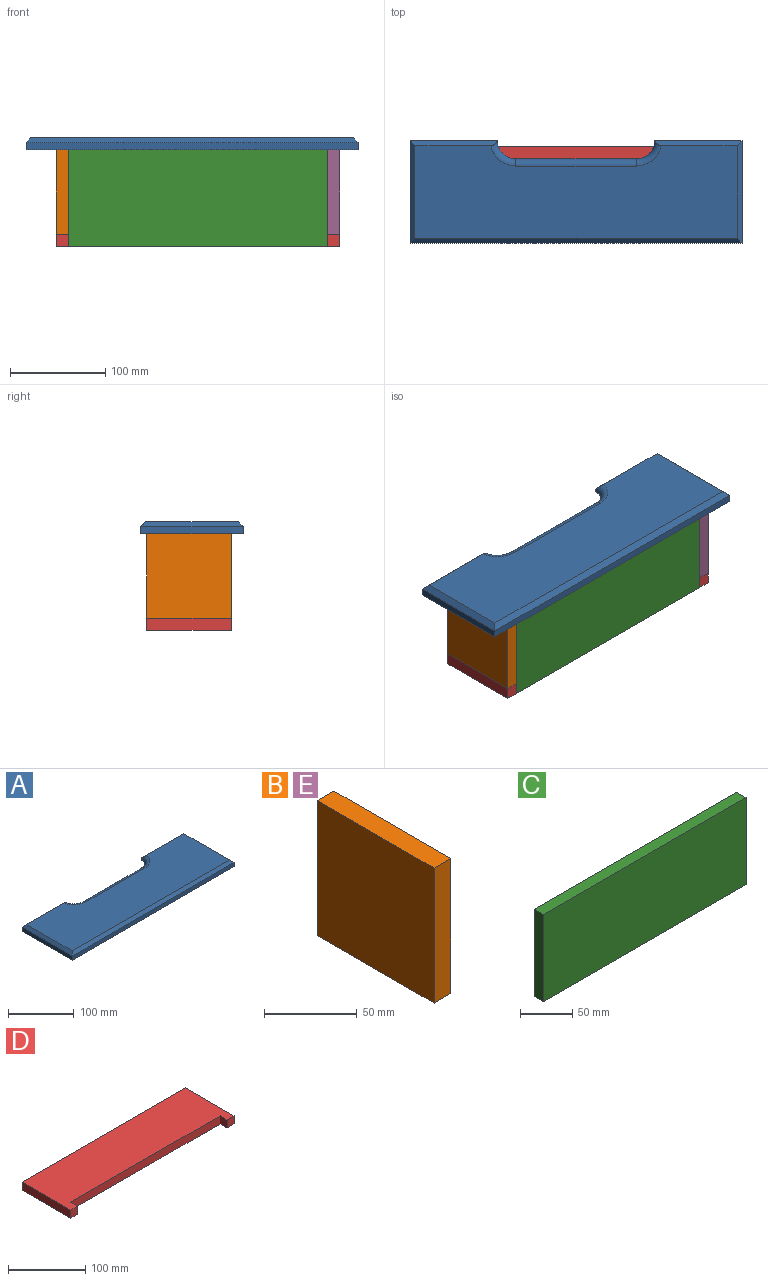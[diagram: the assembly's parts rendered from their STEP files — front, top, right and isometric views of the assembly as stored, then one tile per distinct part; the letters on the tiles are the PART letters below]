
ASSEMBLY  parts=5 mates=4
PART A: 18 faces, bbox 349.3x108x12.7 mm
  f0: plane 91.97x7.62mm, normal (0,1,0), area 688.9mm2, adj f4,f6,f7,f8,f17
  f1: plane 91.97x7.62mm, normal (0,1,0), area 688.9mm2, adj f2,f6,f11,f12,f13
  f2: plane 107.95x7.62mm, normal (-1,0,0), area 822.6mm2, adj f1,f3,f6,f14
  f3: plane 349.25x7.62mm, normal (0,-1,0), area 2661.3mm2, adj f2,f4,f6,f15
  f4: plane 107.95x7.62mm, normal (1,0,0), area 822.6mm2, adj f0,f3,f6,f16
  f5: plane 339.09x97.79mm, normal (0,0,1), area 29569.7mm2, adj f7,f9,f11,f13,f14,f15,f16,f17
  f6: plane 349.25x107.95mm, normal (0,0,-1), area 33197.2mm2, adj f0,f1,f2,f3,f4,f8,f10,f12
  f7: torus R=26.67mm, axis (0,0,1), area 340.9mm2, adj f0,f5,f8,f9,f17
  f8: torus R=26.67mm, axis (0,0,1), area 372mm2, adj f0,f6,f7,f10
  f9: cylinder r=7.62mm len=127mm, axis (1,0,0), area 1358.1mm2, adj f5,f7,f10,f11
  f10: cylinder r=7.62mm len=127mm, axis (-1,0,0), area 1358.1mm2, adj f6,f8,f9,f12
  f11: torus R=26.67mm, axis (0,0,1), area 340.9mm2, adj f1,f5,f9,f12,f13
  f12: torus R=26.67mm, axis (0,0,1), area 372mm2, adj f1,f6,f10,f11
  f13: plane 91.64x5.08mm, normal (0,0.71,0.71), area 627.5mm2, adj f1,f5,f11,f14
  f14: plane 107.95x5.08mm, normal (-0.71,0,0.71), area 739mm2, adj f2,f5,f13,f15
  f15: plane 349.25x5.08mm, normal (0,-0.71,0.71), area 2472.6mm2, adj f3,f5,f14,f16
  f16: plane 107.95x5.08mm, normal (0.71,0,0.71), area 739mm2, adj f4,f5,f15,f17
  f17: plane 91.64x5.08mm, normal (0,0.71,0.71), area 627.5mm2, adj f0,f5,f7,f16
PART B: 6 faces, bbox 12.7x88.9x88.9 mm
  f0: plane 88.9x12.7mm, normal (0,0,-1), area 1129mm2, adj f1,f3,f4,f5
  f1: plane 88.9x12.7mm, normal (0,1,0), area 1129mm2, adj f0,f2,f4,f5
  f2: plane 88.9x12.7mm, normal (0,0,1), area 1129mm2, adj f1,f3,f4,f5
  f3: plane 88.9x12.7mm, normal (0,-1,0), area 1129mm2, adj f0,f2,f4,f5
  f4: plane 88.9x88.9mm, normal (1,0,0), area 7903.2mm2, adj f0,f1,f2,f3
  f5: plane 88.9x88.9mm, normal (-1,0,0), area 7903.2mm2, adj f0,f1,f2,f3
PART C: 6 faces, bbox 273.1x12.7x101.6 mm
  f0: plane 101.6x12.7mm, normal (-1,0,0), area 1290.3mm2, adj f1,f3,f4,f5
  f1: plane 273.05x12.7mm, normal (0,0,-1), area 3467.7mm2, adj f0,f2,f4,f5
  f2: plane 101.6x12.7mm, normal (1,0,0), area 1290.3mm2, adj f1,f3,f4,f5
  f3: plane 273.05x12.7mm, normal (0,0,1), area 3467.7mm2, adj f0,f2,f4,f5
  f4: plane 273.05x101.6mm, normal (0,-1,0), area 27741.9mm2, adj f0,f1,f2,f3
  f5: plane 273.05x101.6mm, normal (0,1,0), area 27741.9mm2, adj f0,f1,f2,f3
PART D: 10 faces, bbox 298.5x88.9x12.7 mm
  f0: plane 12.7x12.7mm, normal (1,0,0), area 161.3mm2, adj f1,f7,f8,f9
  f1: plane 273.05x12.7mm, normal (0,-1,0), area 3467.7mm2, adj f0,f2,f8,f9
  f2: plane 12.7x12.7mm, normal (-1,0,0), area 161.3mm2, adj f1,f3,f8,f9
  f3: plane 12.7x12.7mm, normal (0,-1,0), area 161.3mm2, adj f2,f4,f8,f9
  f4: plane 88.9x12.7mm, normal (1,0,0), area 1129mm2, adj f3,f5,f8,f9
  f5: plane 298.45x12.7mm, normal (0,1,0), area 3790.3mm2, adj f4,f6,f8,f9
  f6: plane 88.9x12.7mm, normal (-1,0,0), area 1129mm2, adj f5,f7,f8,f9
  f7: plane 12.7x12.7mm, normal (0,-1,0), area 161.3mm2, adj f0,f6,f8,f9
  f8: plane 298.45x88.9mm, normal (0,0,1), area 23064.5mm2, adj f0,f1,f2,f3,f4,f5,f6,f7
  f9: plane 298.45x88.9mm, normal (0,0,-1), area 23064.5mm2, adj f0,f1,f2,f3,f4,f5,f6,f7
PART E: same geometry as B
PLACE A t=(6.35,6.35,0)mm
PLACE B t=(-66.01,-183.69,64.79)mm
PLACE C t=(80.24,-284.14,-101.26)mm
PLACE D t=(70.5,-369.56,-101.6)mm
PLACE E t=(219.74,-183.69,64.79)mm
MATE fastened B.f0 <-> D.f8  axis (0,0,-1) through (-66.01,-296.84,-88.9)mm
MATE fastened C.f3 <-> A.f6  axis (0,0,1) through (83.21,-296.84,0)mm
MATE fastened D.f0 <-> C.f0  axis (1,0,0) through (-53.31,-296.84,-101.6)mm
MATE fastened E.f0 <-> D.f8  axis (0,0,-1) through (232.44,-296.84,-88.9)mm
